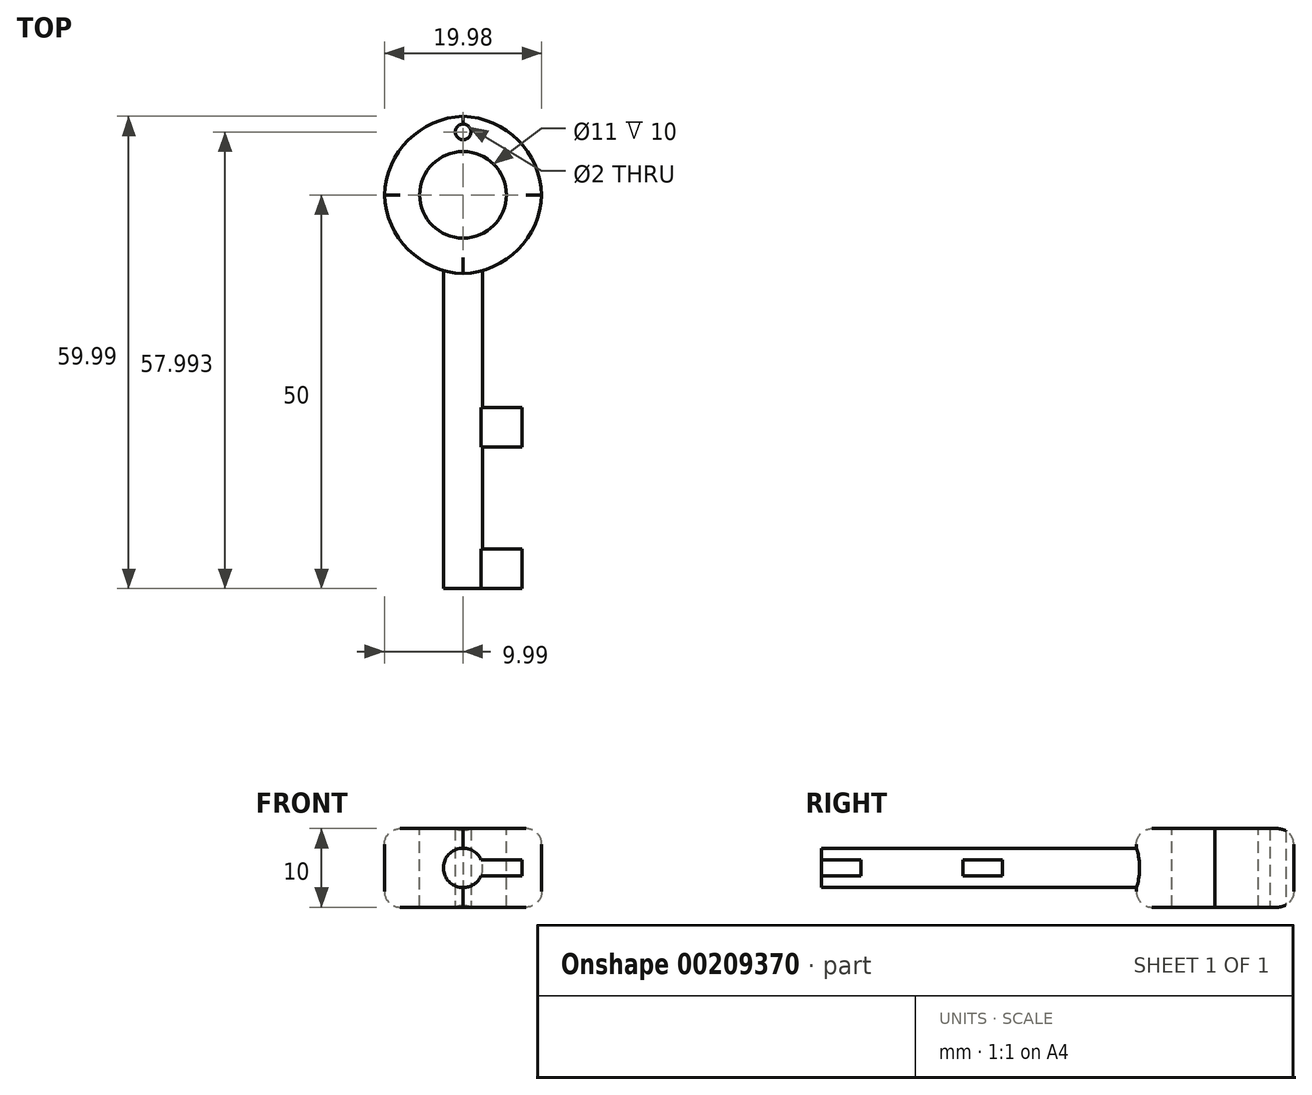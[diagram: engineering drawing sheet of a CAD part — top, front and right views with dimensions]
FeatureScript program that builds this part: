
annotation { "Feature Type Name" : "Feature", "Feature Type Description" : "" }
export const myFeature = defineFeature(function(context is Context, id is Id, definition is map)
    precondition{}
    {
        {
            var Q0;
            Q0=qCreatedBy(makeId("Top.planeOp"),FACE);
            var sketch = newSketch(context, id + "F0", { "sketchPlane" : qUnion([Q0])});
            skLineSegment(sketch, "E0.bottom", {"start": v(10, -10) * mm, "end": v(-10, -10) * mm});
            skLineSegment(sketch, "E0.top", {"start": v(10, 10) * mm, "end": v(-10, 10) * mm});
            skLineSegment(sketch, "E0.left", {"start": v(10, -10) * mm, "end": v(10, 10) * mm});
            skLineSegment(sketch, "E0.right", {"start": v(-10, -10) * mm, "end": v(-10, 10) * mm});
            skPoint(sketch, "E0.middle", {"position": v(0, 0) * mm});
            skSolve(sketch);
        }
        {
            var Q0;
            Q0=makeQuery(id+"F0.imprint","IMPRINT",FACE,{"disambiguationData":[TD([[makeQuery(id+"F0.imprint","IMPRINT",EDGE,{"derivedFrom":sQuery(id+"F0.wireOp",EDGE,"E0.bottom")}),-1.0]])]});
            extrude(context, id + "F1", {"entities" : qUnion([Q0]), "depth" : 10 * mm});
        }
        {
            var Q0;
            Q0=makeQuery(id+"F1.opExtrude","SWEPT_FACE",FACE,{"disambiguationData":[OSD([sQuery(id+"F0.wireOp",EDGE,"E0.bottom")])]});
            var sketch = newSketch(context, id + "F2", { "sketchPlane" : qUnion([Q0])});
            skLineSegment(sketch, "E1.bottom", {"start": v(2.5, 2.5) * mm, "end": v(-2.5, 2.5) * mm});
            skLineSegment(sketch, "E1.top", {"start": v(2.5, 7.5) * mm, "end": v(-2.5, 7.5) * mm});
            skLineSegment(sketch, "E1.left", {"start": v(2.5, 2.5) * mm, "end": v(2.5, 7.5) * mm});
            skLineSegment(sketch, "E1.right", {"start": v(-2.5, 2.5) * mm, "end": v(-2.5, 7.5) * mm});
            skPoint(sketch, "E1.middle", {"position": v(0, 5) * mm});
            skPoint(sketch, "E1.middle.positionSnap0", {"position": v(-10, 5) * mm});
            skPoint(sketch, "E1.centerSnap0", {"position": v(-10, 5) * mm});
            skSolve(sketch);
        }
        {
            var Q0;
            Q0=makeQuery(id+"F2.imprint","IMPRINT",FACE,{"disambiguationData":[TD([[makeQuery(id+"F2.imprint","IMPRINT",EDGE,{"derivedFrom":sQuery(id+"F2.wireOp",EDGE,"E1.bottom")}),-1.0]])]});
            extrude(context, id + "F3", {"entities" : qUnion([Q0]), "operationType" : NewBodyOperationType.ADD, "depth" : 40 * mm});
        }
        {
            var Q0;
            Q0=makeQuery(id+"F3.opExtrude","SWEPT_FACE",FACE,{"disambiguationData":[OSD([sQuery(id+"F2.wireOp",EDGE,"E1.left")])]});
            var sketch = newSketch(context, id + "F4", { "sketchPlane" : qUnion([Q0])});
            skLineSegment(sketch, "E2.bottom", {"start": v(-50, 4) * mm, "end": v(-45, 4) * mm});
            skLineSegment(sketch, "E2.top", {"start": v(-50, 6) * mm, "end": v(-45, 6) * mm});
            skLineSegment(sketch, "E2.left", {"start": v(-50, 4) * mm, "end": v(-50, 6) * mm});
            skLineSegment(sketch, "E2.right", {"start": v(-45, 4) * mm, "end": v(-45, 6) * mm});
            skPoint(sketch, "E2.middle", {"position": v(-47.5, 5) * mm});
            skPoint(sketch, "E2.middle.positionSnap0", {"position": v(-50, 5) * mm});
            skPoint(sketch, "E2.centerSnap0", {"position": v(-50, 5) * mm});
            skLineSegment(sketch, "E3.bottom", {"start": v(-27, 4) * mm, "end": v(-32, 4) * mm});
            skLineSegment(sketch, "E3.top", {"start": v(-27, 6) * mm, "end": v(-32, 6) * mm});
            skLineSegment(sketch, "E3.left", {"start": v(-27, 4) * mm, "end": v(-27, 6) * mm});
            skLineSegment(sketch, "E3.right", {"start": v(-32, 4) * mm, "end": v(-32, 6) * mm});
            skPoint(sketch, "E3.middle", {"position": v(-29.5, 5) * mm});
            skPoint(sketch, "E3.middle.positionSnap0", {"position": v(-45, 5) * mm});
            skPoint(sketch, "E3.centerSnap0", {"position": v(-45, 5) * mm});
            skSolve(sketch);
        }
        {
            var Q0;
            Q0=makeQuery(id+"F4.imprint","IMPRINT",FACE,{"disambiguationData":[TD([[makeQuery(id+"F4.imprint","IMPRINT",EDGE,{"derivedFrom":sQuery(id+"F4.wireOp",EDGE,"E2.bottom")}),1.0]])]});
            var Q1;
            Q1=makeQuery(id+"F4.imprint","IMPRINT",FACE,{"disambiguationData":[TD([[makeQuery(id+"F4.imprint","IMPRINT",EDGE,{"derivedFrom":sQuery(id+"F4.wireOp",EDGE,"E3.bottom")}),-1.0]])]});
            extrude(context, id + "F5", {"entities" : qUnion([Q0, Q1]), "operationType" : NewBodyOperationType.ADD, "depth" : 5 * mm});
        }
        {
            var Q0;
            Q0=makeQuery(id+"F3.opExtrude","SWEPT_EDGE",EDGE,{"disambiguationData":[OSD([sQuery(id+"F2.wireOp",EDGE,"E1.top"),sQuery(id+"F2.wireOp",EDGE,"E1.left")])]});
            var Q1;
            Q1=makeQuery(id+"F3.opExtrude","SWEPT_EDGE",EDGE,{"disambiguationData":[OSD([sQuery(id+"F2.wireOp",EDGE,"E1.top"),sQuery(id+"F2.wireOp",EDGE,"E1.right")])]});
            var Q2;
            Q2=makeQuery(id+"F3.opExtrude","SWEPT_EDGE",EDGE,{"disambiguationData":[OSD([sQuery(id+"F2.wireOp",EDGE,"E1.bottom"),sQuery(id+"F2.wireOp",EDGE,"E1.right")])]});
            var Q3;
            Q3=makeQuery(id+"F3.opExtrude","SWEPT_EDGE",EDGE,{"disambiguationData":[OSD([sQuery(id+"F2.wireOp",EDGE,"E1.bottom"),sQuery(id+"F2.wireOp",EDGE,"E1.left")])]});
            fillet(context, id + "F6", {"entities" : qUnion([Q0, Q1, Q2, Q3]), "radius" : 2.5 * mm, "tangentPropagation" : true, "allowEdgeOverflow" : false});
        }
        {
            var Q0;
            Q0=makeQuery(id+"F1.opExtrude","SWEPT_EDGE",EDGE,{"disambiguationData":[OSD([sQuery(id+"F0.wireOp",EDGE,"E0.top"),sQuery(id+"F0.wireOp",EDGE,"E0.left")])]});
            var Q1;
            Q1=makeQuery(id+"F1.opExtrude","SWEPT_EDGE",EDGE,{"disambiguationData":[OSD([sQuery(id+"F0.wireOp",EDGE,"E0.bottom"),sQuery(id+"F0.wireOp",EDGE,"E0.left")])]});
            var Q2;
            Q2=makeQuery(id+"F1.opExtrude","SWEPT_EDGE",EDGE,{"disambiguationData":[OSD([sQuery(id+"F0.wireOp",EDGE,"E0.top"),sQuery(id+"F0.wireOp",EDGE,"E0.right")])]});
            var Q3;
            Q3=makeQuery(id+"F1.opExtrude","SWEPT_EDGE",EDGE,{"disambiguationData":[OSD([sQuery(id+"F0.wireOp",EDGE,"E0.bottom"),sQuery(id+"F0.wireOp",EDGE,"E0.right")])]});
            fillet(context, id + "F7", {"entities" : qUnion([Q0, Q1, Q2, Q3]), "radius" : 10.38 * mm, "tangentPropagation" : true, "allowEdgeOverflow" : false});
        }
        {
            var Q0;
            Q0=makeQuery(id+"F1.opExtrude","CAP_FACE",FACE,{"disambiguationData":[OSD([sQuery(id+"F0.wireOp",EDGE,"E0.bottom"),sQuery(id+"F0.wireOp",EDGE,"E0.top"),sQuery(id+"F0.wireOp",EDGE,"E0.left"),sQuery(id+"F0.wireOp",EDGE,"E0.right")])],"isStart":true});
            var sketch = newSketch(context, id + "F8", { "sketchPlane" : qUnion([Q0])});
            skCircle(sketch, "E4", {"center": v(0, 0) * mm, "radius": 5.5 * mm});
            skSolve(sketch);
        }
        {
            var Q0;
            Q0=makeQuery(id+"F1.opExtrude","CAP_FACE",FACE,{"disambiguationData":[OSD([sQuery(id+"F0.wireOp",EDGE,"E0.bottom"),sQuery(id+"F0.wireOp",EDGE,"E0.top"),sQuery(id+"F0.wireOp",EDGE,"E0.left"),sQuery(id+"F0.wireOp",EDGE,"E0.right")])],"isStart":false});
            var sketch = newSketch(context, id + "F9", { "sketchPlane" : qUnion([Q0])});
            skCircle(sketch, "E5", {"center": v(0, 0) * mm, "radius": 5.5 * mm});
            skSolve(sketch);
        }
        {
            var Q0;
            Q0=sQuery(id+"F9.wireOp",VERTEX,"E5.center");
            var Q1;
            Q1=makeQuery(id+"F1.opExtrude","SWEPT_BODY",BODY,{"disambiguationData":[OSD([sQuery(id+"F0.wireOp",EDGE,"E0.bottom"),sQuery(id+"F0.wireOp",EDGE,"E0.top"),sQuery(id+"F0.wireOp",EDGE,"E0.left"),sQuery(id+"F0.wireOp",EDGE,"E0.right")])]});
            hole(context, id + "F10", {"style" : HoleStyle.SIMPLE, "endStyle" : HoleEndStyle.THROUGH, "holeDiameter" : 11 * mm, "locations" : qUnion([Q0]), "scope" : qUnion([Q1]), "isTappedThrough" : true});
        }
        {
            var Q0;
            Q0=makeQuery(id+"F8.imprint","IMPRINT",FACE,{"disambiguationData":[TD([[makeQuery(id+"F8.imprint","IMPRINT",EDGE,{"derivedFrom":sQuery(id+"F8.wireOp",EDGE,"E4")}),-1.0]])]});
            var sketch = newSketch(context, id + "F11", { "sketchPlane" : qUnion([Q0])});
            skCircle(sketch, "E6", {"center": v(0, -8) * mm, "radius": 1 * mm});
            skSolve(sketch);
        }
        {
            var Q0;
            Q0=sQuery(id+"F11.wireOp",VERTEX,"E6.center");
            var Q1;
            Q1=makeQuery(id+"F1.opExtrude","SWEPT_BODY",BODY,{"disambiguationData":[OSD([sQuery(id+"F0.wireOp",EDGE,"E0.bottom"),sQuery(id+"F0.wireOp",EDGE,"E0.top"),sQuery(id+"F0.wireOp",EDGE,"E0.left"),sQuery(id+"F0.wireOp",EDGE,"E0.right")])]});
            hole(context, id + "F12", {"style" : HoleStyle.SIMPLE, "endStyle" : HoleEndStyle.THROUGH, "holeDiameter" : 2 * mm, "locations" : qUnion([Q0]), "scope" : qUnion([Q1]), "isTappedThrough" : true});
        }
        {
            var Q0;
            {var subQ0=sQuery(id+"F0.wireOp",EDGE,"E0.left");var subQ1=sQuery(id+"F0.wireOp",EDGE,"E0.top");Q0=makeQuery(id+"F7.opFillet","BLEND_EDGE",EDGE,{"blendedFrom":[makeQuery(id+"F1.opExtrude","SWEPT_EDGE",EDGE,{"disambiguationData":[OSD([subQ1,subQ0])]}),makeQuery(id+"F1.opExtrude","CAP_FACE",FACE,{"disambiguationData":[OSD([sQuery(id+"F0.wireOp",EDGE,"E0.bottom"),subQ1,subQ0,sQuery(id+"F0.wireOp",EDGE,"E0.right")])],"isStart":false})],"blendedInto":[makeQuery(id+"F1.opExtrude","CAP_FACE",FACE,{"disambiguationData":[OSD([sQuery(id+"F0.wireOp",EDGE,"E0.bottom"),subQ1,subQ0,sQuery(id+"F0.wireOp",EDGE,"E0.right")])],"isStart":false})]});}
            var Q1;
            {var subQ0=sQuery(id+"F0.wireOp",EDGE,"E0.right");var subQ1=sQuery(id+"F0.wireOp",EDGE,"E0.bottom");Q1=makeQuery(id+"F7.opFillet","BLEND_EDGE",EDGE,{"blendedFrom":[makeQuery(id+"F1.opExtrude","SWEPT_EDGE",EDGE,{"disambiguationData":[OSD([subQ1,subQ0])]}),makeQuery(id+"F1.opExtrude","CAP_FACE",FACE,{"disambiguationData":[OSD([subQ1,sQuery(id+"F0.wireOp",EDGE,"E0.top"),sQuery(id+"F0.wireOp",EDGE,"E0.left"),subQ0])],"isStart":true})],"blendedInto":[makeQuery(id+"F1.opExtrude","CAP_FACE",FACE,{"disambiguationData":[OSD([subQ1,sQuery(id+"F0.wireOp",EDGE,"E0.top"),sQuery(id+"F0.wireOp",EDGE,"E0.left"),subQ0])],"isStart":true})]});}
            var Q2;
            {var subQ0=sQuery(id+"F0.wireOp",EDGE,"E0.right");var subQ1=sQuery(id+"F0.wireOp",EDGE,"E0.bottom");Q2=makeQuery(id+"F7.opFillet","BLEND_EDGE",EDGE,{"blendedFrom":[makeQuery(id+"F1.opExtrude","SWEPT_EDGE",EDGE,{"disambiguationData":[OSD([subQ1,subQ0])]}),makeQuery(id+"F1.opExtrude","CAP_FACE",FACE,{"disambiguationData":[OSD([subQ1,sQuery(id+"F0.wireOp",EDGE,"E0.top"),sQuery(id+"F0.wireOp",EDGE,"E0.left"),subQ0])],"isStart":false})],"blendedInto":[makeQuery(id+"F1.opExtrude","CAP_FACE",FACE,{"disambiguationData":[OSD([subQ1,sQuery(id+"F0.wireOp",EDGE,"E0.top"),sQuery(id+"F0.wireOp",EDGE,"E0.left"),subQ0])],"isStart":false})]});}
            var Q3;
            {var subQ0=sQuery(id+"F0.wireOp",EDGE,"E0.left");var subQ1=sQuery(id+"F0.wireOp",EDGE,"E0.bottom");Q3=makeQuery(id+"F7.opFillet","BLEND_EDGE",EDGE,{"blendedFrom":[makeQuery(id+"F1.opExtrude","SWEPT_EDGE",EDGE,{"disambiguationData":[OSD([subQ1,subQ0])]}),makeQuery(id+"F1.opExtrude","CAP_FACE",FACE,{"disambiguationData":[OSD([subQ1,sQuery(id+"F0.wireOp",EDGE,"E0.top"),subQ0,sQuery(id+"F0.wireOp",EDGE,"E0.right")])],"isStart":false})],"blendedInto":[makeQuery(id+"F1.opExtrude","CAP_FACE",FACE,{"disambiguationData":[OSD([subQ1,sQuery(id+"F0.wireOp",EDGE,"E0.top"),subQ0,sQuery(id+"F0.wireOp",EDGE,"E0.right")])],"isStart":false})]});}
            var Q4;
            Q4=makeQuery(id+"F10.hole-0.boolean.opBoolean","COPY",EDGE,{"derivedFrom":makeQuery(id+"F10.hole-0.opRevolve","SWEPT_EDGE",EDGE,{"disambiguationData":[OSD([sQuery(id+"F10.hole-0.sketch.wireOp",EDGE,"core_line_2"),sQuery(id+"F10.hole-0.sketch.wireOp",EDGE,"core_line_3")])]})});
            var Q5;
            {var subQ0=sQuery(id+"F0.wireOp",EDGE,"E0.right");var subQ1=sQuery(id+"F0.wireOp",EDGE,"E0.top");Q5=makeQuery(id+"F7.opFillet","BLEND_EDGE",EDGE,{"blendedFrom":[makeQuery(id+"F1.opExtrude","SWEPT_EDGE",EDGE,{"disambiguationData":[OSD([subQ1,subQ0])]}),makeQuery(id+"F1.opExtrude","CAP_FACE",FACE,{"disambiguationData":[OSD([sQuery(id+"F0.wireOp",EDGE,"E0.bottom"),subQ1,sQuery(id+"F0.wireOp",EDGE,"E0.left"),subQ0])],"isStart":false})],"blendedInto":[makeQuery(id+"F1.opExtrude","CAP_FACE",FACE,{"disambiguationData":[OSD([sQuery(id+"F0.wireOp",EDGE,"E0.bottom"),subQ1,sQuery(id+"F0.wireOp",EDGE,"E0.left"),subQ0])],"isStart":false})]});}
            var Q6;
            {var subQ0=sQuery(id+"F0.wireOp",EDGE,"E0.left");var subQ1=sQuery(id+"F0.wireOp",EDGE,"E0.bottom");Q6=makeQuery(id+"F7.opFillet","BLEND_EDGE",EDGE,{"blendedFrom":[makeQuery(id+"F1.opExtrude","SWEPT_EDGE",EDGE,{"disambiguationData":[OSD([subQ1,subQ0])]}),makeQuery(id+"F1.opExtrude","CAP_FACE",FACE,{"disambiguationData":[OSD([subQ1,sQuery(id+"F0.wireOp",EDGE,"E0.top"),subQ0,sQuery(id+"F0.wireOp",EDGE,"E0.right")])],"isStart":true})],"blendedInto":[makeQuery(id+"F1.opExtrude","CAP_FACE",FACE,{"disambiguationData":[OSD([subQ1,sQuery(id+"F0.wireOp",EDGE,"E0.top"),subQ0,sQuery(id+"F0.wireOp",EDGE,"E0.right")])],"isStart":true})]});}
            var Q7;
            {var subQ0=sQuery(id+"F0.wireOp",EDGE,"E0.left");var subQ1=sQuery(id+"F0.wireOp",EDGE,"E0.top");Q7=makeQuery(id+"F7.opFillet","BLEND_EDGE",EDGE,{"blendedFrom":[makeQuery(id+"F1.opExtrude","SWEPT_EDGE",EDGE,{"disambiguationData":[OSD([subQ1,subQ0])]}),makeQuery(id+"F1.opExtrude","CAP_FACE",FACE,{"disambiguationData":[OSD([sQuery(id+"F0.wireOp",EDGE,"E0.bottom"),subQ1,subQ0,sQuery(id+"F0.wireOp",EDGE,"E0.right")])],"isStart":true})],"blendedInto":[makeQuery(id+"F1.opExtrude","CAP_FACE",FACE,{"disambiguationData":[OSD([sQuery(id+"F0.wireOp",EDGE,"E0.bottom"),subQ1,subQ0,sQuery(id+"F0.wireOp",EDGE,"E0.right")])],"isStart":true})]});}
            var Q8;
            {var subQ0=sQuery(id+"F0.wireOp",EDGE,"E0.right");var subQ1=sQuery(id+"F0.wireOp",EDGE,"E0.top");Q8=makeQuery(id+"F7.opFillet","BLEND_EDGE",EDGE,{"blendedFrom":[makeQuery(id+"F1.opExtrude","SWEPT_EDGE",EDGE,{"disambiguationData":[OSD([subQ1,subQ0])]}),makeQuery(id+"F1.opExtrude","CAP_FACE",FACE,{"disambiguationData":[OSD([sQuery(id+"F0.wireOp",EDGE,"E0.bottom"),subQ1,sQuery(id+"F0.wireOp",EDGE,"E0.left"),subQ0])],"isStart":true})],"blendedInto":[makeQuery(id+"F1.opExtrude","CAP_FACE",FACE,{"disambiguationData":[OSD([sQuery(id+"F0.wireOp",EDGE,"E0.bottom"),subQ1,sQuery(id+"F0.wireOp",EDGE,"E0.left"),subQ0])],"isStart":true})]});}
            var Q9;
            Q9=makeQuery(id+"F10.hole-0.boolean.opBoolean","INTERSECT",EDGE,{"derivedFrom":[makeQuery(id+"F1.opExtrude","CAP_FACE",FACE,{"disambiguationData":[OSD([sQuery(id+"F0.wireOp",EDGE,"E0.bottom"),sQuery(id+"F0.wireOp",EDGE,"E0.top"),sQuery(id+"F0.wireOp",EDGE,"E0.left"),sQuery(id+"F0.wireOp",EDGE,"E0.right")])],"isStart":true}),makeQuery(id+"F10.hole-0.opRevolve","SWEPT_FACE",FACE,{"disambiguationData":[OSD([sQuery(id+"F10.hole-0.sketch.wireOp",EDGE,"core_line_2")])]})]});
            fillet(context, id + "F13", {"entities" : qUnion([Q0, Q1, Q2, Q3, Q4, Q5, Q6, Q7, Q8, Q9]), "radius" : 2 * mm, "tangentPropagation" : true, "allowEdgeOverflow" : false});
        }
    });
